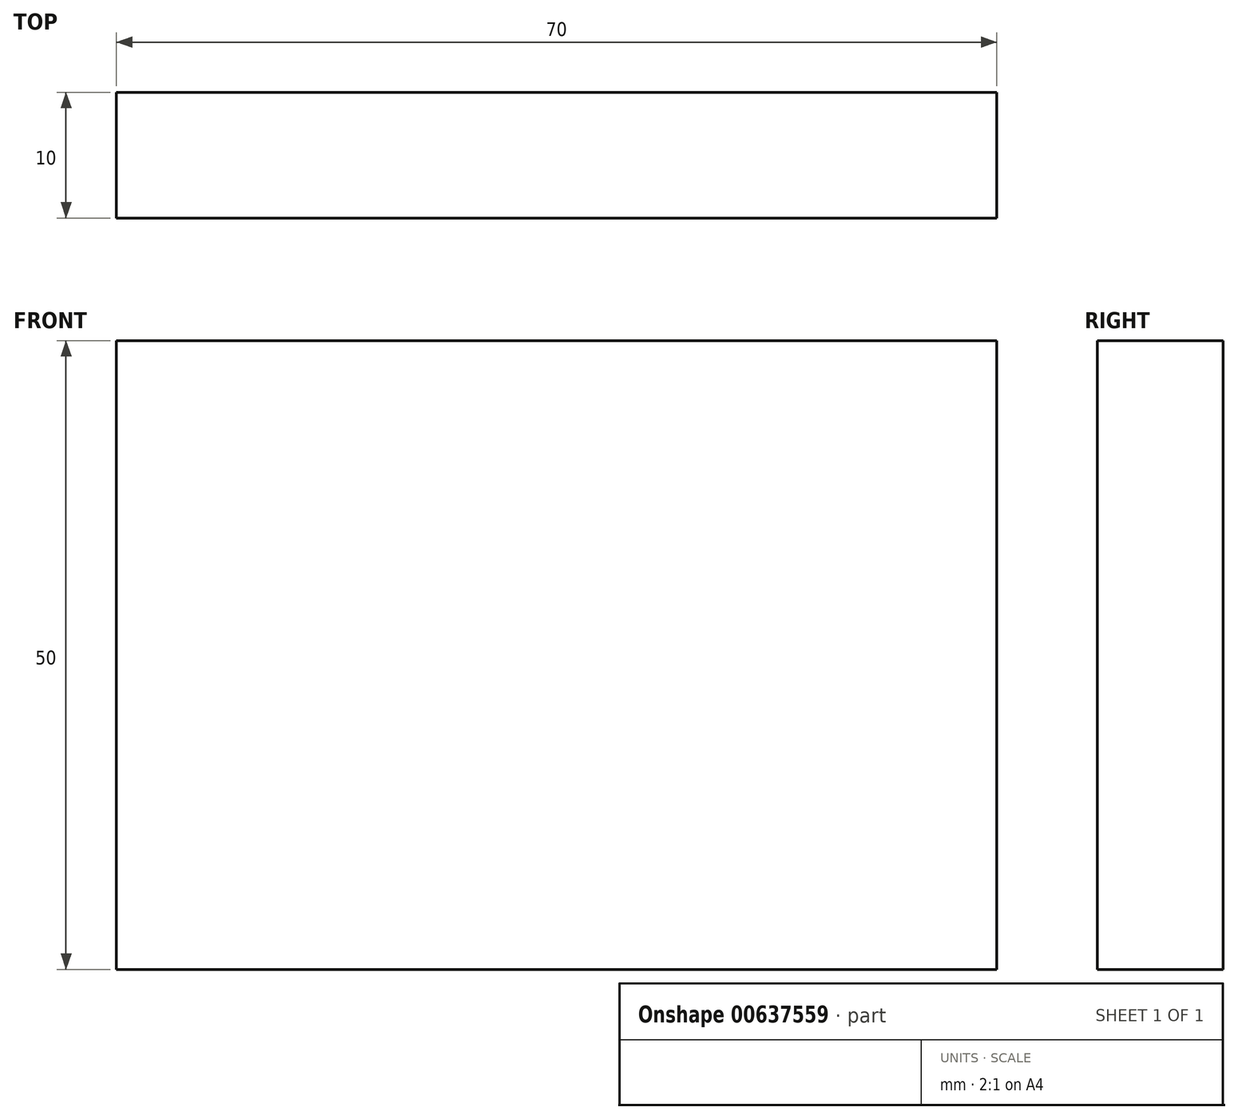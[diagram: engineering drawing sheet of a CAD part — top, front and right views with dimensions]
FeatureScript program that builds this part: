
annotation { "Feature Type Name" : "Feature", "Feature Type Description" : "" }
export const myFeature = defineFeature(function(context is Context, id is Id, definition is map)
    precondition{}
    {
        {
            var Q0;
            Q0=qCreatedBy(makeId("Front.planeOp"),FACE);
            var sketch = newSketch(context, id + "F0", { "sketchPlane" : qUnion([Q0])});
            skLineSegment(sketch, "E0.bottom", {"start": v(-35, -25) * mm, "end": v(35, -25) * mm});
            skLineSegment(sketch, "E0.top", {"start": v(-35, 25) * mm, "end": v(35, 25) * mm});
            skLineSegment(sketch, "E0.left", {"start": v(-35, -25) * mm, "end": v(-35, 25) * mm});
            skLineSegment(sketch, "E0.right", {"start": v(35, -25) * mm, "end": v(35, 25) * mm});
            skPoint(sketch, "E0.middle", {"position": v(0, 0) * mm});
            skSolve(sketch);
        }
        {
            var Q0;
            Q0=makeQuery(id+"F0.imprint","IMPRINT",FACE,{"disambiguationData":[TD([[makeQuery(id+"F0.imprint","IMPRINT",EDGE,{"derivedFrom":sQuery(id+"F0.wireOp",EDGE,"E0.bottom")}),1.0]])]});
            extrude(context, id + "F1", {"entities" : qUnion([Q0]), "endBound" : BoundingType.SYMMETRIC, "depth" : 10 * mm, "offsetDistance" : 25 * mm});
        }
    });
